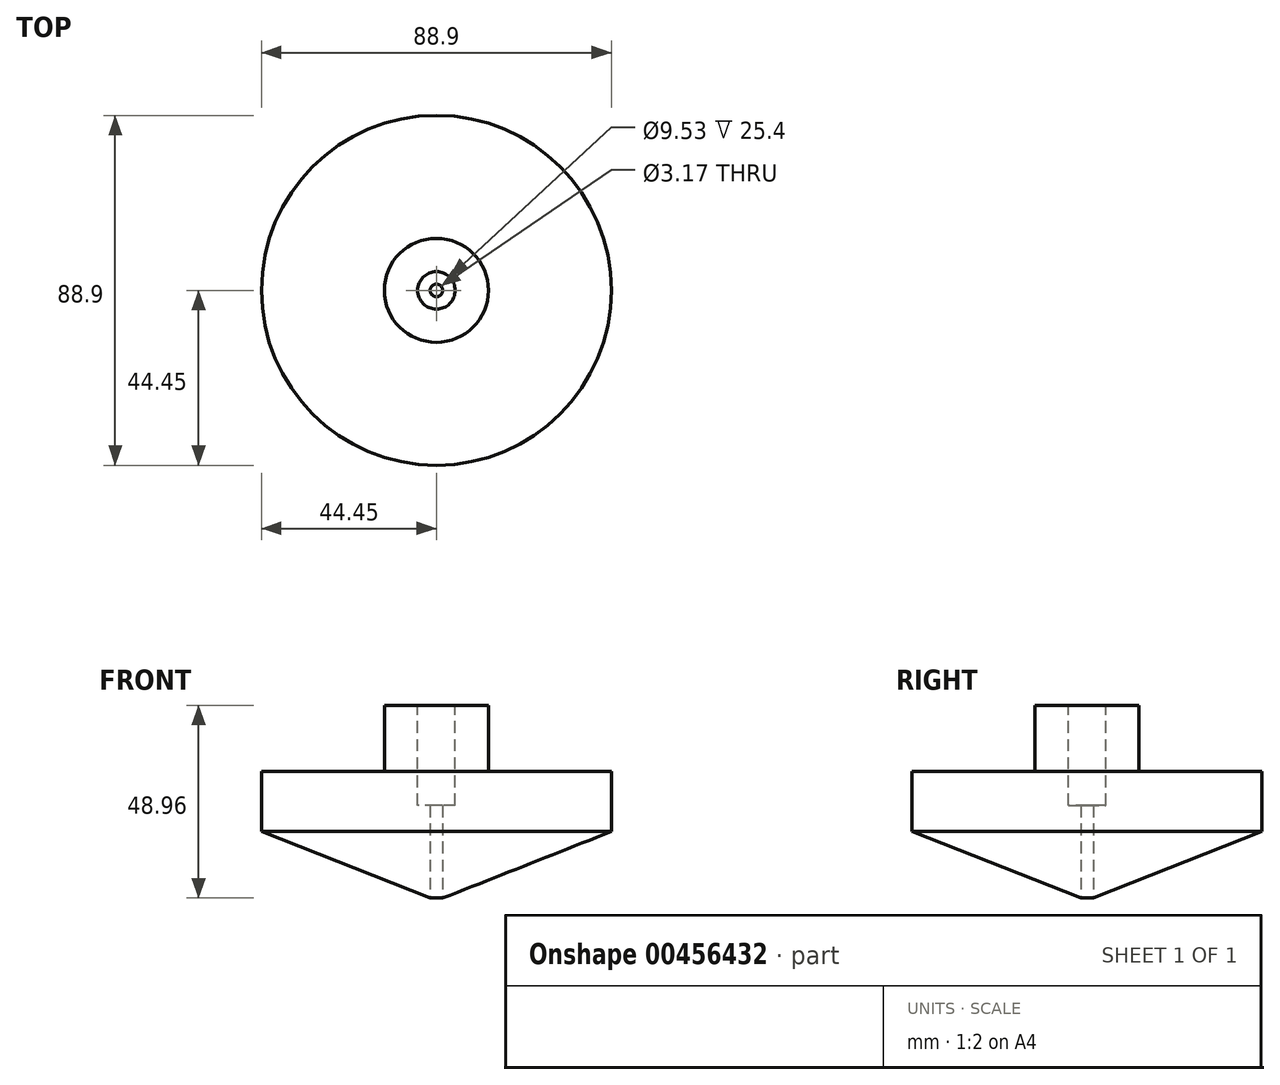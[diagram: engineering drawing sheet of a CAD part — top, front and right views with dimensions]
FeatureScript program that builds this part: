
annotation { "Feature Type Name" : "Feature", "Feature Type Description" : "" }
export const myFeature = defineFeature(function(context is Context, id is Id, definition is map)
    precondition{}
    {
        {
            var Q0;
            Q0=qCreatedBy(makeId("Front.planeOp"),FACE);
            var sketch = newSketch(context, id + "F0", { "sketchPlane" : qUnion([Q0])});
            skLineSegment(sketch, "E0", {"start": v(0, 0) * mm, "end": v(44.45, 17.54) * mm});
            skLineSegment(sketch, "E1", {"start": v(44.45, 17.54) * mm, "end": v(44.45, 32.85) * mm});
            skLineSegment(sketch, "E2", {"start": v(44.45, 32.85) * mm, "end": v(13.2, 32.85) * mm});
            skLineSegment(sketch, "E3", {"start": v(13.2, 32.85) * mm, "end": v(13.2, 49.6) * mm});
            skLineSegment(sketch, "E4", {"start": v(13.2, 49.6) * mm, "end": v(0, 49.6) * mm});
            skLineSegment(sketch, "E5", {"start": v(0, 0) * mm, "end": v(0, 49.6) * mm});
            skLineSegment(sketch, "E6", {"start": v(0, 24.8) * mm, "end": v(44.45, 24.8) * mm});
            skSolve(sketch);
        }
        {
            var Q0;
            Q0=qSketchRegion(id+"F0",true);
            var Q1;
            Q1=sQuery(id+"F0.wireOp",EDGE,"E5");
            revolve(context, id + "F1", {"entities" : qUnion([Q0]), "axis" : qUnion([Q1]), "revolveType" : RevolveType.FULL});
        }
        {
            var Q0;
            Q0=makeQuery(id+"F1.opRevolve","SWEPT_FACE",FACE,{"disambiguationData":[OSD([sQuery(id+"F0.wireOp",EDGE,"E4")])]});
            var sketch = newSketch(context, id + "F2", { "sketchPlane" : qUnion([Q0])});
            skCircle(sketch, "E7", {"center": v(0, 0) * mm, "radius": 4.76 * mm});
            skSolve(sketch);
        }
        {
            var Q0;
            Q0=makeQuery(id+"F2.imprint","IMPRINT",FACE,{"disambiguationData":[TD([[makeQuery(id+"F2.imprint","IMPRINT",EDGE,{"derivedFrom":sQuery(id+"F2.wireOp",EDGE,"E7")}),1.0]])]});
            var sketch = newSketch(context, id + "F3", { "sketchPlane" : qUnion([Q0])});
            skSolve(sketch);
        }
        {
            var Q0;
            Q0=qSketchRegion(id+"F3",true);
            var Q1;
            Q1=makeQuery(id+"F2.imprint","IMPRINT",FACE,{"disambiguationData":[TD([[makeQuery(id+"F2.imprint","IMPRINT",EDGE,{"derivedFrom":sQuery(id+"F2.wireOp",EDGE,"E7")}),1.0]])]});
            extrude(context, id + "F4", {"entities" : qUnion([Q0, Q1]), "operationType" : NewBodyOperationType.REMOVE, "oppositeDirection" : true, "depth" : 25.4 * mm});
        }
        {
            var Q0;
            Q0=qCreatedBy(makeId("Top.planeOp"),FACE);
            var sketch = newSketch(context, id + "F5", { "sketchPlane" : qUnion([Q0])});
            skCircle(sketch, "E8", {"center": v(0, 0) * mm, "radius": 1.6 * mm});
            skCircle(sketch, "E9", {"center": v(0, 0) * mm, "radius": 1.59 * mm});
            skSolve(sketch);
        }
        {
            var Q0;
            Q0=makeQuery(id+"F5.imprint","IMPRINT",FACE,{"disambiguationData":[TD([[makeQuery(id+"F5.imprint","IMPRINT",EDGE,{"derivedFrom":sQuery(id+"F5.wireOp",EDGE,"E9")}),1.0]])]});
            extrude(context, id + "F6", {"entities" : qUnion([Q0]), "operationType" : NewBodyOperationType.REMOVE, "depth" : 25.4 * mm});
        }
    });
